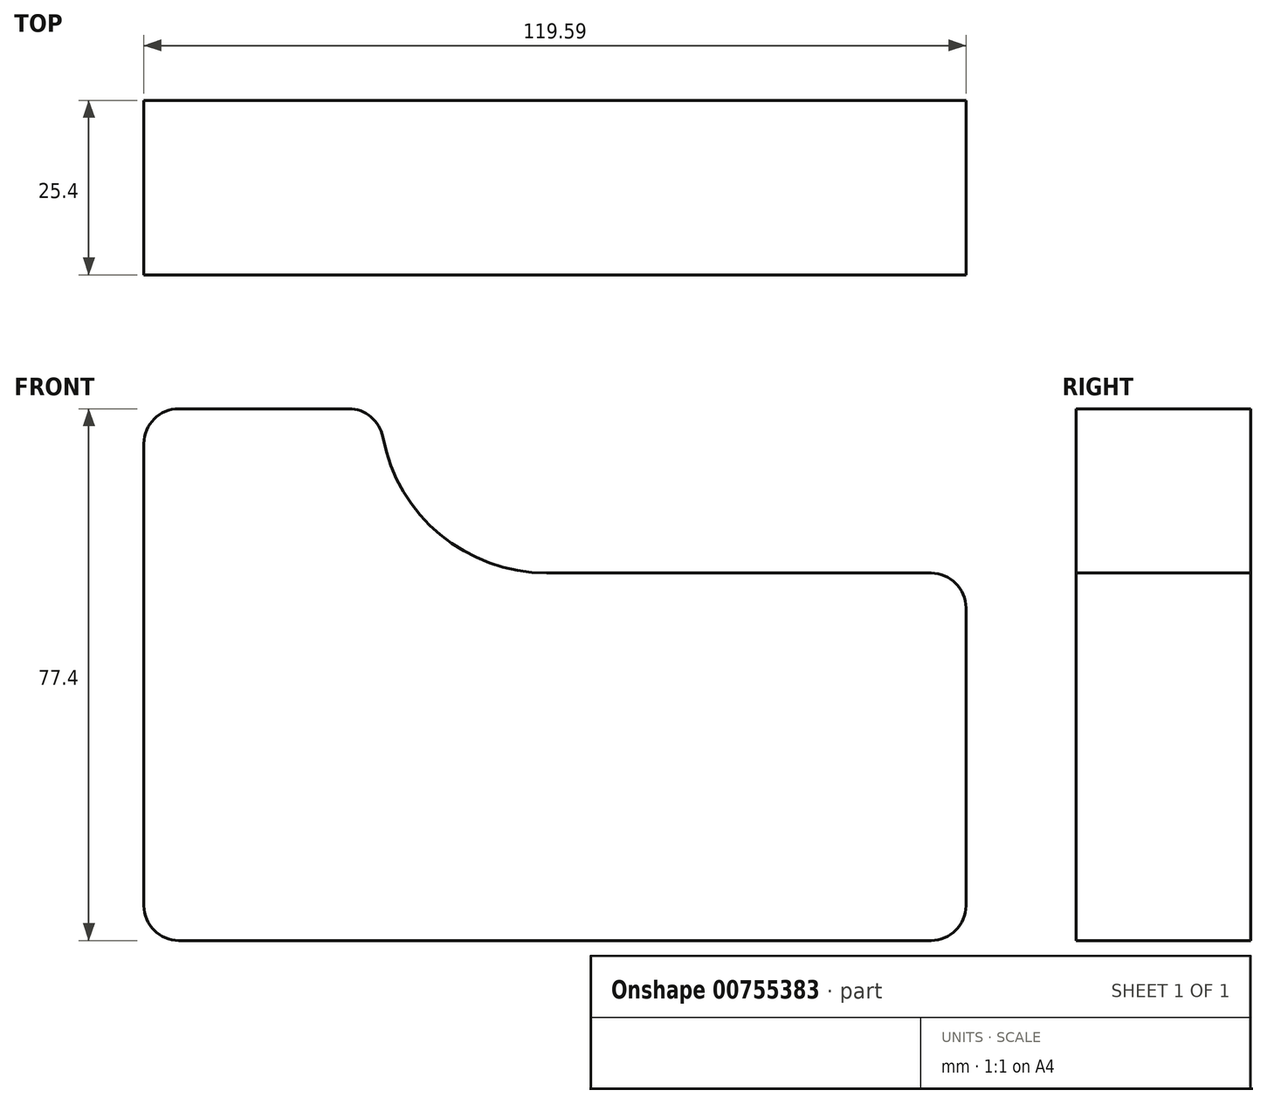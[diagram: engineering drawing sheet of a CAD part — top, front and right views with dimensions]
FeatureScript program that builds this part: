
annotation { "Feature Type Name" : "Feature", "Feature Type Description" : "" }
export const myFeature = defineFeature(function(context is Context, id is Id, definition is map)
    precondition{}
    {
        {
            var Q0;
            Q0=qCreatedBy(makeId("Front.planeOp"),FACE);
            var sketch = newSketch(context, id + "F0", { "sketchPlane" : qUnion([Q0])});
            skLineSegment(sketch, "E0", {"start": v(-58.6, 34.46) * mm, "end": v(-58.6, -42.94) * mm});
            skLineSegment(sketch, "E1", {"start": v(-58.6, -42.94) * mm, "end": v(61, -42.94) * mm});
            skLineSegment(sketch, "E2", {"start": v(61, -42.94) * mm, "end": v(61, 10.55) * mm});
            skLineSegment(sketch, "E3", {"start": v(61, 10.55) * mm, "end": v(0, 10.55) * mm});
            skLineSegment(sketch, "E4", {"start": v(-58.6, 34.46) * mm, "end": v(-24.24, 34.46) * mm});
            skArc(sketch, "E5", {"start": v(0, 10.55) * mm, "mid": v(-17.03, 17.53) * mm, "end": v(-24.24, 34.46) * mm});
            skSolve(sketch);
        }
        {
            var Q0;
            Q0=makeQuery(id+"F0.imprint","IMPRINT",FACE,{"disambiguationData":[TD([[makeQuery(id+"F0.imprint","IMPRINT",EDGE,{"derivedFrom":sQuery(id+"F0.wireOp",EDGE,"E0")}),1.0]])]});
            extrude(context, id + "F1", {"entities" : qUnion([Q0]), "endBound" : BoundingType.SYMMETRIC, "depth" : 25.4 * mm, "offsetDistance" : 25.4 * mm});
        }
        {
            var Q0;
            Q0=makeQuery(id+"F1.opExtrude","SWEPT_EDGE",EDGE,{"disambiguationData":[OSD([sQuery(id+"F0.wireOp",EDGE,"E0"),sQuery(id+"F0.wireOp",EDGE,"E4")])]});
            var Q1;
            Q1=makeQuery(id+"F1.opExtrude","SWEPT_EDGE",EDGE,{"disambiguationData":[OSD([sQuery(id+"F0.wireOp",EDGE,"E2"),sQuery(id+"F0.wireOp",EDGE,"E3")])]});
            var Q2;
            Q2=makeQuery(id+"F1.opExtrude","SWEPT_EDGE",EDGE,{"disambiguationData":[OSD([sQuery(id+"F0.wireOp",EDGE,"E1"),sQuery(id+"F0.wireOp",EDGE,"E2")])]});
            fillet(context, id + "F2", {"entities" : qUnion([Q0, Q1, Q2]), "radius" : 5.08 * mm, "tangentPropagation" : true, "allowEdgeOverflow" : false});
        }
        {
            var Q0;
            Q0=makeQuery(id+"F1.opExtrude","SWEPT_EDGE",EDGE,{"disambiguationData":[OSD([sQuery(id+"F0.wireOp",EDGE,"E0"),sQuery(id+"F0.wireOp",EDGE,"E1")])]});
            var Q1;
            Q1=makeQuery(id+"F1.opExtrude","SWEPT_EDGE",EDGE,{"disambiguationData":[OSD([sQuery(id+"F0.wireOp",EDGE,"E4"),sQuery(id+"F0.wireOp",EDGE,"E5")])]});
            fillet(context, id + "F3", {"entities" : qUnion([Q0, Q1]), "radius" : 5.08 * mm, "tangentPropagation" : true, "allowEdgeOverflow" : false});
        }
    });
